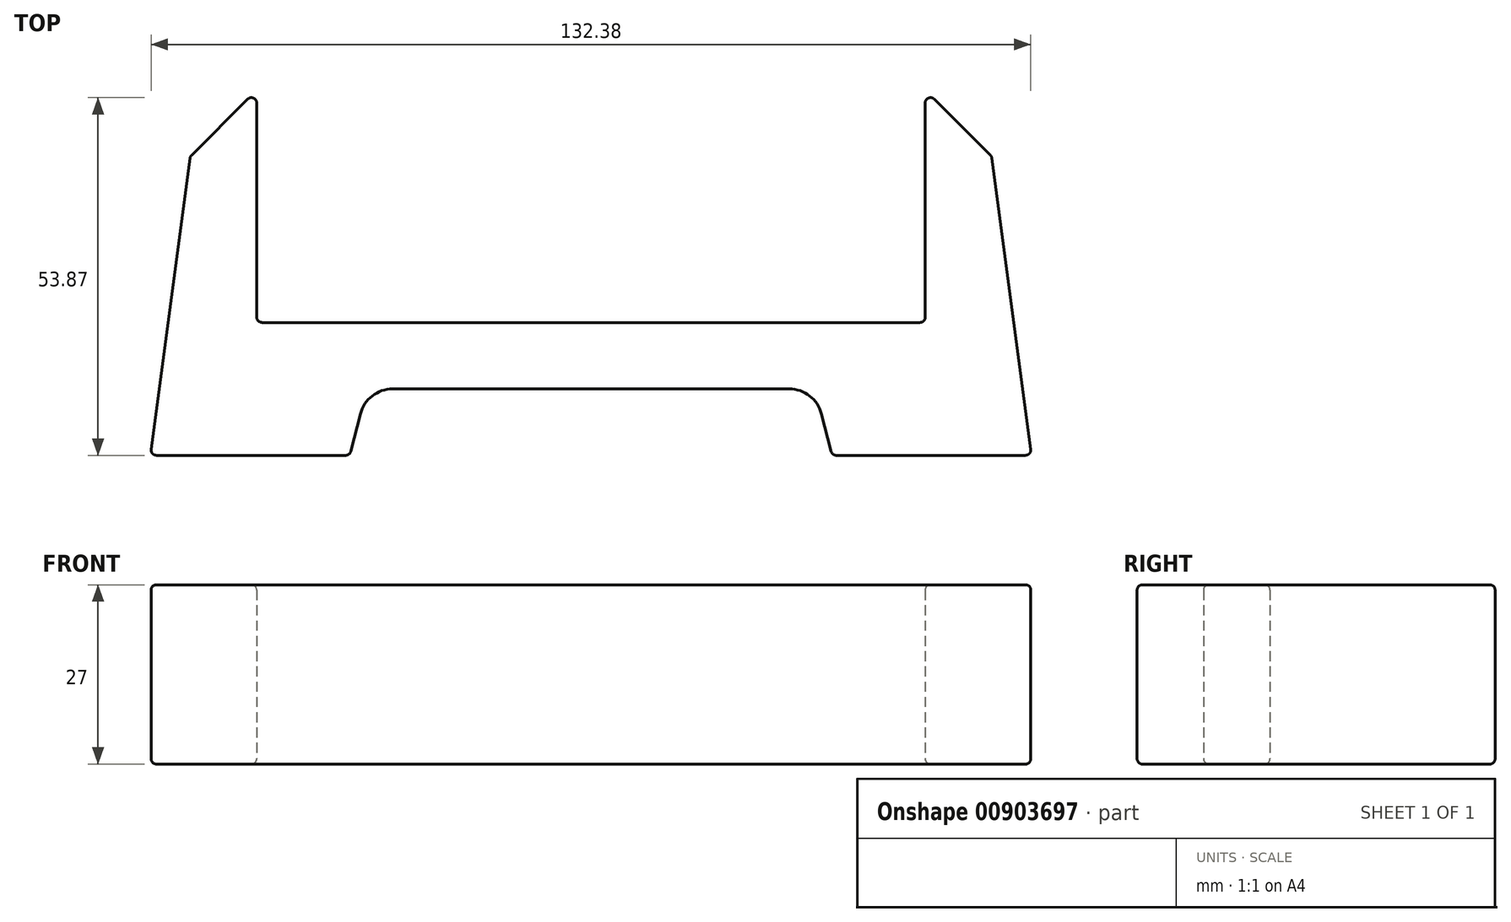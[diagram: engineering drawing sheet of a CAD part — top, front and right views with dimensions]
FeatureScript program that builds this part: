
annotation { "Feature Type Name" : "Feature", "Feature Type Description" : "" }
export const myFeature = defineFeature(function(context is Context, id is Id, definition is map)
    precondition{}
    {
        {
            var Q0;
            Q0=qCreatedBy(makeId("Top.planeOp"),FACE);
            var sketch = newSketch(context, id + "F0", { "sketchPlane" : qUnion([Q0])});
            skLineSegment(sketch, "E0", {"start": v(-50.3, 35) * mm, "end": v(-50.3, 0) * mm});
            skLineSegment(sketch, "E1", {"start": v(-50.3, 0) * mm, "end": v(50.3, 0) * mm});
            skLineSegment(sketch, "E2", {"start": v(50.3, 0) * mm, "end": v(50.3, 35) * mm});
            skLineSegment(sketch, "E3", {"start": v(50.3, 35) * mm, "end": v(60.3, 25) * mm});
            skLineSegment(sketch, "E4", {"start": v(60.3, 25) * mm, "end": v(66.3, -20) * mm});
            skLineSegment(sketch, "E5", {"start": v(66.3, -20) * mm, "end": v(36.3, -20) * mm});
            skLineSegment(sketch, "E6", {"start": v(36.3, -20) * mm, "end": v(34.69, -13.75) * mm});
            skLineSegment(sketch, "E7", {"start": v(29.85, -10) * mm, "end": v(-29.85, -10) * mm});
            skLineSegment(sketch, "E8", {"start": v(-34.69, -13.75) * mm, "end": v(-36.3, -20) * mm});
            skLineSegment(sketch, "E9", {"start": v(-36.3, -20) * mm, "end": v(-66.3, -20) * mm});
            skLineSegment(sketch, "E10", {"start": v(-66.3, -20) * mm, "end": v(-60.3, 25) * mm});
            skLineSegment(sketch, "E11", {"start": v(-60.3, 25) * mm, "end": v(-50.3, 35) * mm});
            skLineSegment(sketch, "E12", {"start": v(0, 0) * mm, "end": v(0, 90.39) * mm, "construction": true});
            skPoint(sketch, "E13.visualSharp", {"position": v(33.72, -10) * mm});
            skArc(sketch, "E13.filletArc", {"start": v(34.69, -13.75) * mm, "mid": v(32.9, -11.05) * mm, "end": v(29.85, -10) * mm});
            skPoint(sketch, "E14.visualSharp", {"position": v(-33.72, -10) * mm});
            skArc(sketch, "E14.filletArc", {"start": v(-29.85, -10) * mm, "mid": v(-32.9, -11.05) * mm, "end": v(-34.69, -13.75) * mm});
            skSolve(sketch);
        }
        {
            var Q0;
            Q0 = qSketchRegion(id + "F0", true);
            extrude(context, id + "F1", {"entities" : qUnion([Q0]), "depth" : 27 * mm, "offsetDistance" : 25 * mm});
        }
        {
            var Q0;
            Q0=makeQuery(id+"F1.opExtrude","CAP_EDGE",EDGE,{"disambiguationData":[OSD([sQuery(id+"F0.wireOp",EDGE,"E7")])],"isStart":false});
            var Q1;
            Q1=makeQuery(id+"F1.opExtrude","CAP_EDGE",EDGE,{"disambiguationData":[OSD([sQuery(id+"F0.wireOp",EDGE,"E6")])],"isStart":false});
            var Q2;
            Q2=makeQuery(id+"F1.opExtrude","CAP_EDGE",EDGE,{"disambiguationData":[OSD([sQuery(id+"F0.wireOp",EDGE,"E13.filletArc")])],"isStart":false});
            var Q3;
            Q3=makeQuery(id+"F1.opExtrude","CAP_EDGE",EDGE,{"disambiguationData":[OSD([sQuery(id+"F0.wireOp",EDGE,"E5")])],"isStart":false});
            var Q4;
            Q4=makeQuery(id+"F1.opExtrude","CAP_EDGE",EDGE,{"disambiguationData":[OSD([sQuery(id+"F0.wireOp",EDGE,"E4")])],"isStart":false});
            var Q5;
            Q5=makeQuery(id+"F1.opExtrude","CAP_FACE",FACE,{"disambiguationData":[OSD([sQuery(id+"F0.wireOp",EDGE,"E0"),sQuery(id+"F0.wireOp",EDGE,"E1"),sQuery(id+"F0.wireOp",EDGE,"E2"),sQuery(id+"F0.wireOp",EDGE,"E3"),sQuery(id+"F0.wireOp",EDGE,"E4"),sQuery(id+"F0.wireOp",EDGE,"E5"),sQuery(id+"F0.wireOp",EDGE,"E6"),sQuery(id+"F0.wireOp",EDGE,"E7"),sQuery(id+"F0.wireOp",EDGE,"E8"),sQuery(id+"F0.wireOp",EDGE,"E9"),sQuery(id+"F0.wireOp",EDGE,"E10"),sQuery(id+"F0.wireOp",EDGE,"E11"),sQuery(id+"F0.wireOp",EDGE,"E13.filletArc"),sQuery(id+"F0.wireOp",EDGE,"E14.filletArc")])],"isStart":false});
            var Q6;
            Q6=makeQuery(id+"F1.opExtrude","SWEPT_FACE",FACE,{"disambiguationData":[OSD([sQuery(id+"F0.wireOp",EDGE,"E4")])]});
            var Q7;
            Q7=makeQuery(id+"F1.opExtrude","SWEPT_FACE",FACE,{"disambiguationData":[OSD([sQuery(id+"F0.wireOp",EDGE,"E5")])]});
            var Q8;
            Q8=makeQuery(id+"F1.opExtrude","SWEPT_FACE",FACE,{"disambiguationData":[OSD([sQuery(id+"F0.wireOp",EDGE,"E8")])]});
            var Q9;
            Q9=makeQuery(id+"F1.opExtrude","SWEPT_FACE",FACE,{"disambiguationData":[OSD([sQuery(id+"F0.wireOp",EDGE,"E9")])]});
            var Q10;
            Q10=makeQuery(id+"F1.opExtrude","SWEPT_FACE",FACE,{"disambiguationData":[OSD([sQuery(id+"F0.wireOp",EDGE,"E7")])]});
            var Q11;
            Q11=makeQuery(id+"F1.opExtrude","SWEPT_FACE",FACE,{"disambiguationData":[OSD([sQuery(id+"F0.wireOp",EDGE,"E0")])]});
            var Q12;
            Q12=makeQuery(id+"F1.opExtrude","SWEPT_FACE",FACE,{"disambiguationData":[OSD([sQuery(id+"F0.wireOp",EDGE,"E3")])]});
            var Q13;
            Q13=makeQuery(id+"F1.opExtrude","CAP_FACE",FACE,{"disambiguationData":[OSD([sQuery(id+"F0.wireOp",EDGE,"E0"),sQuery(id+"F0.wireOp",EDGE,"E1"),sQuery(id+"F0.wireOp",EDGE,"E2"),sQuery(id+"F0.wireOp",EDGE,"E3"),sQuery(id+"F0.wireOp",EDGE,"E4"),sQuery(id+"F0.wireOp",EDGE,"E5"),sQuery(id+"F0.wireOp",EDGE,"E6"),sQuery(id+"F0.wireOp",EDGE,"E7"),sQuery(id+"F0.wireOp",EDGE,"E8"),sQuery(id+"F0.wireOp",EDGE,"E9"),sQuery(id+"F0.wireOp",EDGE,"E10"),sQuery(id+"F0.wireOp",EDGE,"E11"),sQuery(id+"F0.wireOp",EDGE,"E13.filletArc"),sQuery(id+"F0.wireOp",EDGE,"E14.filletArc")])],"isStart":true});
            var Q14;
            Q14=makeQuery(id+"F1.opExtrude","SWEPT_EDGE",EDGE,{"disambiguationData":[OSD([sQuery(id+"F0.wireOp",EDGE,"E1"),sQuery(id+"F0.wireOp",EDGE,"E2")])]});
            var Q15;
            Q15=makeQuery(id+"F1.opExtrude","SWEPT_EDGE",EDGE,{"disambiguationData":[OSD([sQuery(id+"F0.wireOp",EDGE,"E10"),sQuery(id+"F0.wireOp",EDGE,"E11")])]});
            fillet(context, id + "F2", {"entities" : qUnion([Q0, Q1, Q2, Q3, Q4, Q5, Q6, Q7, Q8, Q9, Q10, Q11, Q12, Q13, Q14, Q15]), "radius" : .8 * mm, "tangentPropagation" : true, "allowEdgeOverflow" : false});
        }
    });
